# Revit family: Drain_Trench_12_Inch_Wide-Zurn-Z665-Heavy-Duty
name_source: partatom
category: Plumbing Fixtures
units: mm (PartAtom-declared; Revit-internal decimal feet)

## family parameters
Always vertical = Yes
Cut with Voids When Loaded = No
Maintain Annotation Orientation = No
OmniClass Number = 23.70.50.21.24.14
OmniClass Title = Deck Waste Water Drains
Part Type = Normal
Room Calculation Point = No
Round Connector Dimension = Use Radius
Shared = No
Work Plane-Based = No

## types (24) — shared parameters
Assembly Code = D2020.30
CW Connection = No
Default Elevation = 2 "
Description = 12[305] WIDE MODULAR TRENCH DRAIN, HEAVY-DUTY
Grate Open Area (Sq. In.) = 110 SF
HW Connection = No
Main Material = Iron - Zurn - Cast - Painted - Blue
Manufacturer = Zurn Water, LLC
Manufacurer Brand = Zurn
Modified Date = 11/24/25
Product Documentation Link = https://files.zurn.com
Product Installation Sheet URL = https://files.zurn.com
Product Page URL = https://www.zurn.com
Product data url = https://www.bimobject.com
URL = www.zurn.com
Vent Connection = No
WFU = 1
Waste Connection = Yes
zero-valued in all types: CWFU, HWFU

## per-type parameters (varying)
| type | A_ Pipe Size (Inner Diameter) | A_ Pipe Size (Nominal Diameter) | A_ Pipe Size (Nominal Radius) | A_ Pipe Size (Outer Diameter) | Actual Body Height 'E' | Approx. Weight (Lbs) | Body Height 'E' | Grate Material | Model | Top flange height | Type Comments | ZB/ZN |
| Z665-2IC | 2.067 " | 2 " | 1 " | 2.375 " | 13.188 " | 100 " | 13.188 " | Iron - Zurn - Cast - Painted - Blue | Z665 | 2 " | Z665 2 Inch Inside Caulk Outlet | 0 " |
| Z665-3IC | 3.068 " | 3 " | 1.5 " | 3.5 " | 13.188 " | 100 " | 13.188 " | Iron - Zurn - Cast - Painted - Blue | Z665 | 2 " | Z665 3 Inch Inside Caulk Outlet | 0 " |
| Z665-4IC | 4.026 " | 4 " | 2 " | 4.5 " | 13.188 " | 100 " | 13.188 " | Iron - Zurn - Cast - Painted - Blue | Z665 | 2 " | Z665 4 Inch Inside Caulk Outlet | 0 " |
| Z665-5IC | 5.047 " | 5 " | 2.5 " | 5.563 " | 13.188 " | 110 " | 13.188 " | Iron - Zurn - Cast - Painted - Blue | Z665 | 2 " | Z665 5 Inch Inside Caulk Outlet | 0 " |
| Z665-6IC | 6.065 " | 6 " | 3 " | 6.625 " | 13.188 " | 110 " | 13.188 " | Iron - Zurn - Cast - Painted - Blue | Z665 | 2 " | Z665 6 Inch Inside Caulk Outlet | 0 " |
| ZB665-2IC | 2.067 " | 2 " | 1 " | 2.375 " | 13.313 " | 100 " | 13.188 " | Bronze - Zurn - Polished | ZB665 | 2.125 " | ZB665 2 Inch Inside Caulk Outlet | 0.125 " |
| ZB665-3IC | 3.068 " | 3 " | 1.5 " | 3.5 " | 13.313 " | 100 " | 13.188 " | Bronze - Zurn - Polished | ZB665 | 2.125 " | ZB665 3 Inch Inside Caulk Outlet | 0.125 " |
| ZB665-4IC | 4.026 " | 4 " | 2 " | 4.5 " | 13.313 " | 100 " | 13.188 " | Bronze - Zurn - Polished | ZB665 | 2.125 " | ZB665 4 Inch Inside Caulk Outlet | 0.125 " |
| ZB665-5IC | 5.047 " | 5 " | 2.5 " | 5.563 " | 13.313 " | 110 " | 13.188 " | Bronze - Zurn - Polished | ZB665 | 2.125 " | ZB665 5 Inch Inside Caulk Outlet | 0.125 " |
| ZB665-6IC | 6.065 " | 6 " | 3 " | 6.625 " | 13.313 " | 110 " | 13.188 " | Bronze - Zurn - Polished | ZB665 | 2.125 " | ZB665 6 Inch Inside Caulk Outlet | 0.125 " |
| ZN665-2IC | 2.067 " | 2 " | 1 " | 2.375 " | 13.188 " | 100 " | 13.188 " | Steel - Zurn -Stainless - Polished | ZN665 | 2.125 " | ZN665 2 Inch Inside Caulk Outlet | 0 " |
| ZN665-3IC | 3.068 " | 3 " | 1.5 " | 3.5 " | 13.188 " | 100 " | 13.188 " | Steel - Zurn -Stainless - Polished | ZN665 | 2.125 " | ZN665 3 Inch Inside Caulk Outlet | 0 " |
| ZN665-4IC | 4.026 " | 4 " | 2 " | 4.5 " | 13.188 " | 100 " | 13.188 " | Steel - Zurn -Stainless - Polished | ZN665 | 2.125 " | ZN665 4 Inch Inside Caulk Outlet | 0 " |
| ZN665-5IC | 5.047 " | 5 " | 2.5 " | 5.563 " | 13.188 " | 110 " | 13.188 " | Steel - Zurn -Stainless - Polished | ZN665 | 2.125 " | ZN665 5 Inch Inside Caulk Outlet | 0 " |
| ZN665-6IC | 6.065 " | 6 " | 3 " | 6.625 " | 13.188 " | 110 " | 13.188 " | Steel - Zurn -Stainless - Polished | ZN665 | 2.125 " | ZN665 6 Inch Inside Caulk Outlet | 0 " |
| Z665-2NL | 2.067 " | 2 " | 1 " | 2.375 " | 12.5 " | 100 " | 12.5 " | Iron - Zurn - Cast - Painted - Blue | Z665 | 2 " | Z665 2 Inch Neo-Loc Outlet | 0 " |
| Z665-3NL | 3.068 " | 3 " | 1.5 " | 3.5 " | 12.5 " | 100 " | 12.5 " | Iron - Zurn - Cast - Painted - Blue | Z665 | 2 " | Z665 3 Inch Neo-Loc Outlet | 0 " |
| Z665-4NL | 4.026 " | 4 " | 2 " | 4.5 " | 12.5 " | 100 " | 12.5 " | Iron - Zurn - Cast - Painted - Blue | Z665 | 2 " | Z665 4 Inch Neo-Loc Outlet | 0 " |
| ZB665-2NL | 2.067 " | 2 " | 1 " | 2.375 " | 12.625 " | 100 " | 12.5 " | Bronze - Zurn - Polished | ZB665 | 2.125 " | ZB665 2 Inch Neo-Loc Outlet | 0.125 " |
| ZB665-3NL | 3.068 " | 3 " | 1.5 " | 3.5 " | 12.625 " | 100 " | 12.5 " | Bronze - Zurn - Polished | ZB665 | 2.125 " | ZB665 3 Inch Neo-Loc Outlet | 0.125 " |
| ZB665-4NL | 4.026 " | 4 " | 2 " | 4.5 " | 12.625 " | 100 " | 12.5 " | Bronze - Zurn - Polished | ZB665 | 2.125 " | ZB665 4 Inch Neo-Loc Outlet | 0.125 " |
| ZN665-2NL | 2.067 " | 2 " | 1 " | 2.375 " | 12.5 " | 100 " | 12.5 " | Steel - Zurn -Stainless - Polished | ZN665 | 2.125 " | ZN665 2 Inch Neo-Loc Outlet | 0 " |
| ZN665-3NL | 3.068 " | 3 " | 1.5 " | 3.5 " | 12.5 " | 100 " | 12.5 " | Steel - Zurn -Stainless - Polished | ZN665 | 2.125 " | ZN665 3 Inch Neo-Loc Outlet | 0 " |
| ZN665-4NL | 4.026 " | 4 " | 2 " | 4.5 " | 12.5 " | 100 " | 12.5 " | Steel - Zurn -Stainless - Polished | ZN665 | 2.125 " | ZN665 4 Inch Neo-Loc Outlet | 0 " |

## geometry (parser evidence)
native form markers: Sweep x9
no freeform markers — native parametric forms only
